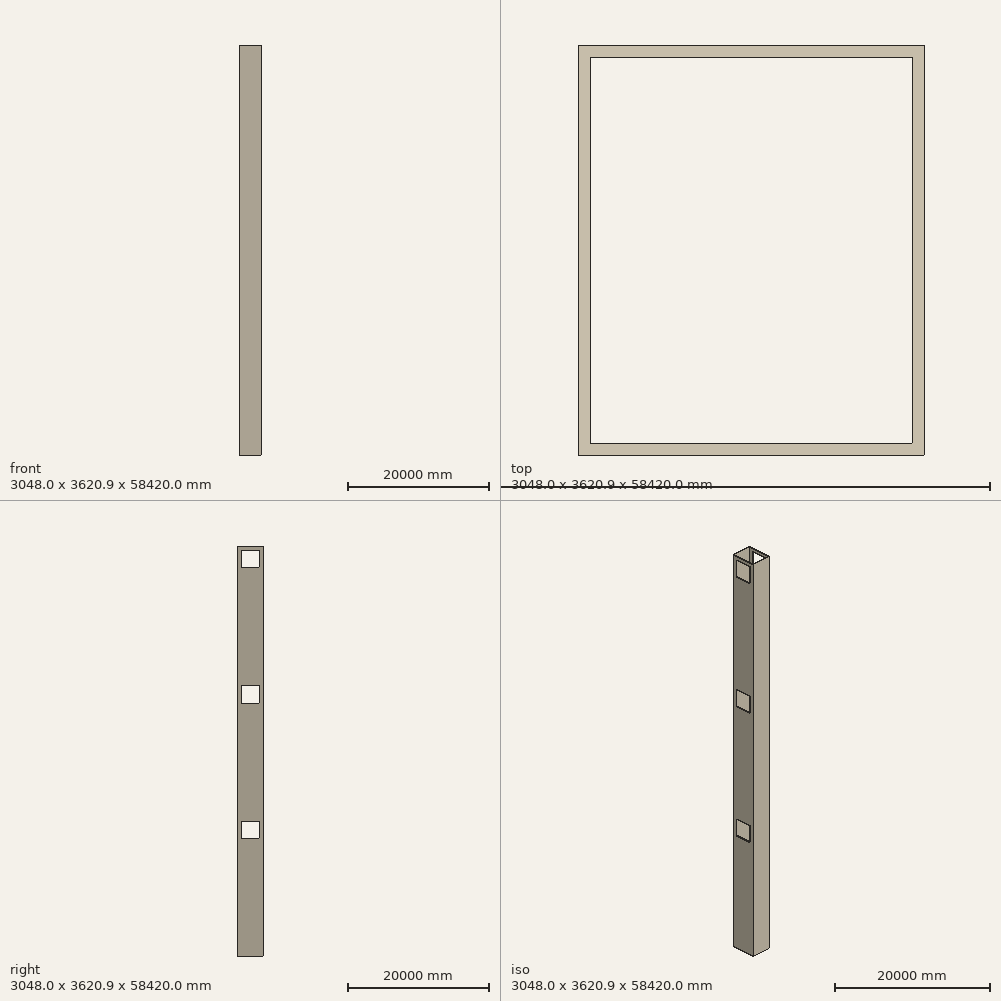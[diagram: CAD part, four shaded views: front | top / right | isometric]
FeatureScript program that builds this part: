
annotation { "Feature Type Name" : "Feature", "Feature Type Description" : "" }
export const myFeature = defineFeature(function(context is Context, id is Id, definition is map)
    precondition{}
    {
        {
            var Q0;
            Q0=qCreatedBy(makeId("Top.planeOp"),FACE);
            var sketch = newSketch(context, id + "F0", { "sketchPlane" : qUnion([Q0])});
            skLineSegment(sketch, "E0.bottom", {"start": v(0, 0) * mm, "end": v(3048, 0) * mm});
            skLineSegment(sketch, "E0.top", {"start": v(0, 3620.86) * mm, "end": v(3048, 3620.86) * mm});
            skLineSegment(sketch, "E0.left", {"start": v(0, 0) * mm, "end": v(0, 3620.86) * mm});
            skLineSegment(sketch, "E0.right", {"start": v(3048, 0) * mm, "end": v(3048, 3620.86) * mm});
            skLineSegment(sketch, "E1.bottom", {"start": v(101.6, 101.6) * mm, "end": v(2946.4, 101.6) * mm});
            skLineSegment(sketch, "E1.top", {"start": v(101.6, 3519.26) * mm, "end": v(2946.4, 3519.26) * mm});
            skLineSegment(sketch, "E1.left", {"start": v(101.6, 101.6) * mm, "end": v(101.6, 3519.26) * mm});
            skLineSegment(sketch, "E1.right", {"start": v(2946.4, 101.6) * mm, "end": v(2946.4, 3519.26) * mm});
            skSolve(sketch);
        }
        {
            var Q0;
            Q0=makeQuery(id+"F0.imprint","IMPRINT",FACE,{"disambiguationData":[TD([[makeQuery(id+"F0.imprint","IMPRINT",EDGE,{"derivedFrom":sQuery(id+"F0.wireOp",EDGE,"E0.bottom")}),1.0]])]});
            extrude(context, id + "F1", {"entities" : qUnion([Q0]), "depth" : 58420 * mm});
        }
        {
            var Q0;
            Q0=makeQuery(id+"F1.opExtrude","SWEPT_FACE",FACE,{"disambiguationData":[OSD([sQuery(id+"F0.wireOp",EDGE,"E0.right")])]});
            var sketch = newSketch(context, id + "F2", { "sketchPlane" : qUnion([Q0])});
            skLineSegment(sketch, "E2.bottom", {"start": v(508, 57912) * mm, "end": v(3048, 57912) * mm});
            skLineSegment(sketch, "E2.top", {"start": v(508, 55372) * mm, "end": v(3048, 55372) * mm});
            skLineSegment(sketch, "E2.left", {"start": v(508, 57912) * mm, "end": v(508, 55372) * mm});
            skLineSegment(sketch, "E2.right", {"start": v(3048, 57912) * mm, "end": v(3048, 55372) * mm});
            skLineSegment(sketch, "E3.bottom", {"start": v(508, 38608) * mm, "end": v(3048, 38608) * mm});
            skLineSegment(sketch, "E3.top", {"start": v(508, 36068) * mm, "end": v(3048, 36068) * mm});
            skLineSegment(sketch, "E3.left", {"start": v(508, 38608) * mm, "end": v(508, 36068) * mm});
            skLineSegment(sketch, "E3.right", {"start": v(3048, 38608) * mm, "end": v(3048, 36068) * mm});
            skLineSegment(sketch, "E4.bottom", {"start": v(508, 19304) * mm, "end": v(3048, 19304) * mm});
            skLineSegment(sketch, "E4.top", {"start": v(508, 16764) * mm, "end": v(3048, 16764) * mm});
            skLineSegment(sketch, "E4.left", {"start": v(508, 19304) * mm, "end": v(508, 16764) * mm});
            skLineSegment(sketch, "E4.right", {"start": v(3048, 19304) * mm, "end": v(3048, 16764) * mm});
            skSolve(sketch);
        }
        {
            var Q0;
            Q0=makeQuery(id+"F2.imprint","IMPRINT",FACE,{"disambiguationData":[TD([[makeQuery(id+"F2.imprint","IMPRINT",EDGE,{"derivedFrom":sQuery(id+"F2.wireOp",EDGE,"E4.bottom")}),-1.0]])]});
            var Q1;
            Q1=makeQuery(id+"F2.imprint","IMPRINT",FACE,{"disambiguationData":[TD([[makeQuery(id+"F2.imprint","IMPRINT",EDGE,{"derivedFrom":sQuery(id+"F2.wireOp",EDGE,"E2.bottom")}),-1.0]])]});
            var Q2;
            Q2=makeQuery(id+"F2.imprint","IMPRINT",FACE,{"disambiguationData":[TD([[makeQuery(id+"F2.imprint","IMPRINT",EDGE,{"derivedFrom":sQuery(id+"F2.wireOp",EDGE,"E3.bottom")}),-1.0]])]});
            extrude(context, id + "F3", {"entities" : qUnion([Q0, Q1, Q2]), "operationType" : NewBodyOperationType.REMOVE, "oppositeDirection" : true, "depth" : 3810 * mm});
        }
    });
